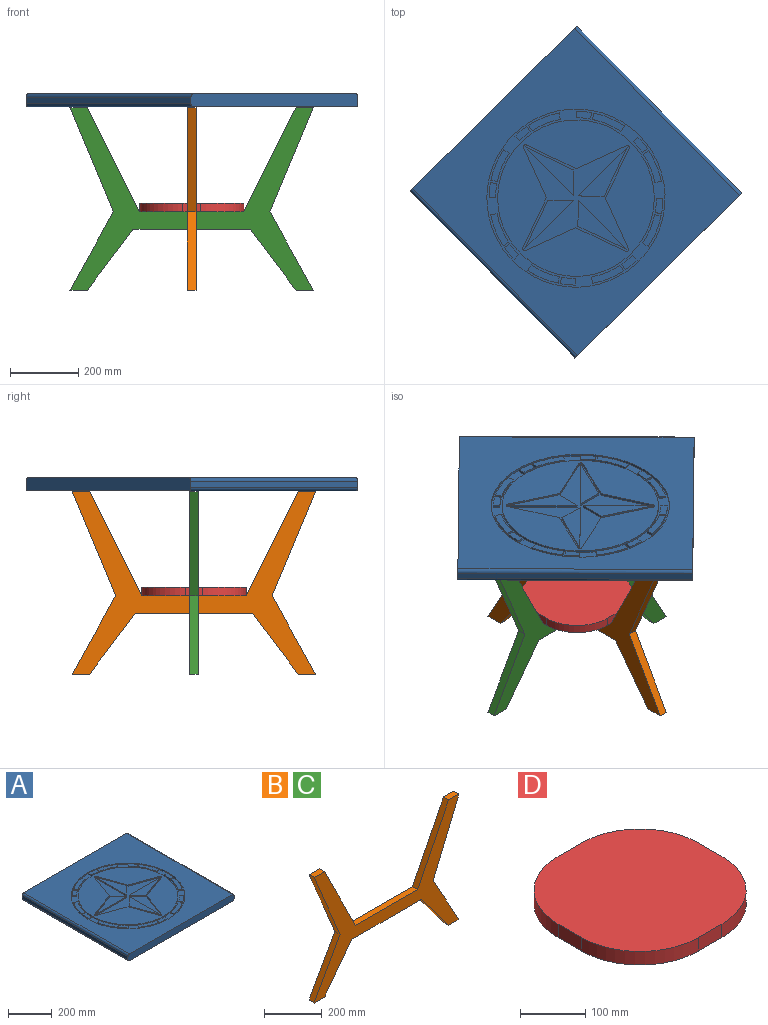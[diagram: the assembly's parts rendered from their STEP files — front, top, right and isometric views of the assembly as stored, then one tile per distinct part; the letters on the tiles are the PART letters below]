
ASSEMBLY  parts=4 mates=2
PART A: 123 faces, bbox 685.8x685.8x38.1 mm
  f0: plane 457.2x457.2mm, normal (0,0,1), area 108640mm2, adj f76,f96,f97,f98,f99,f100,f101,f102
  f1: plane 685.8x666.75mm, normal (0,0,1), area 244313.3mm2, adj f3,f5,f9,f10,f59
  f2: plane 685.8x19.05mm, normal (-1,0,0), area 13064.5mm2, adj f3,f5,f8,f10
  f3: plane 685.8x38.1mm, normal (0,-1,0), area 26051.1mm2, adj f1,f2,f4,f6,f7,f8,f9,f10
  f4: plane 685.8x19.05mm, normal (1,0,0), area 13064.5mm2, adj f3,f5,f7,f9
  f5: plane 685.8x38.1mm, normal (0,1,0), area 26051.1mm2, adj f1,f2,f4,f6,f7,f8,f9,f10
  f6: plane 685.8x666.75mm, normal (0,0,-1), area 457257.1mm2, adj f3,f5,f7,f8
  f7: cylinder r=9.53mm len=685.8mm, axis (0,1,0), area 10260.8mm2, adj f3,f4,f5,f6
  f8: cylinder r=9.53mm len=685.8mm, axis (0,-1,0), area 10260.8mm2, adj f2,f3,f5,f6
  f9: cylinder r=9.53mm len=685.8mm, axis (0,-1,0), area 10260.8mm2, adj f1,f3,f4,f5
  f10: cylinder r=9.53mm len=685.8mm, axis (0,1,0), area 10260.8mm2, adj f1,f2,f3,f5
  f11: cylinder r=254mm len=90.1mm, axis (0,0,1), area 623.1mm2, adj f12,f60,f77,f93
  f12: plane 18.77x6.35mm, normal (0.17,-0.98,0), area 121mm2, adj f11,f13,f77,f93
  f13: cylinder r=234.95mm len=82.47mm, axis (0,0,1), area 570.3mm2, adj f12,f60,f77,f93
  f14: cylinder r=254mm len=33.92mm, axis (0,0,1), area 281.5mm2, adj f15,f61,f77,f92
  f15: plane 15.61x10.93mm, normal (0.57,-0.82,0), area 121mm2, adj f14,f16,f77,f92
  f16: cylinder r=234.95mm len=31.37mm, axis (0,0,1), area 260.4mm2, adj f15,f61,f77,f92
  f17: cylinder r=254mm len=33.92mm, axis (0,0,1), area 281.5mm2, adj f18,f62,f77,f91
  f18: plane 15.61x10.93mm, normal (0.82,0.57,0), area 121mm2, adj f17,f19,f77,f91
  f19: cylinder r=234.95mm len=31.37mm, axis (0,0,1), area 260.4mm2, adj f18,f62,f77,f91
  f20: cylinder r=254mm len=90.1mm, axis (0,0,1), area 623.1mm2, adj f21,f63,f77,f90
  f21: plane 15.61x10.93mm, normal (0.57,0.82,0), area 121mm2, adj f20,f22,f77,f90
  f22: cylinder r=234.95mm len=82.47mm, axis (0,0,1), area 570.3mm2, adj f21,f63,f77,f90
  f23: cylinder r=254mm len=44.11mm, axis (0,0,1), area 281.5mm2, adj f24,f64,f77,f89
  f24: plane 18.76x6.35mm, normal (0.17,0.98,0), area 121mm2, adj f23,f25,f77,f89
  f25: cylinder r=234.95mm len=40.8mm, axis (0,0,1), area 260.4mm2, adj f24,f64,f77,f89
  f26: cylinder r=254mm len=90.1mm, axis (0,0,1), area 623.1mm2, adj f27,f65,f77,f88
  f27: plane 18.77x6.35mm, normal (-0.17,0.98,0), area 121mm2, adj f26,f28,f77,f88
  f28: cylinder r=234.95mm len=82.47mm, axis (0,0,1), area 570.3mm2, adj f27,f65,f77,f88
  f29: cylinder r=254mm len=33.92mm, axis (0,0,1), area 281.5mm2, adj f30,f66,f77,f87
  f30: plane 15.61x10.93mm, normal (-0.57,0.82,0), area 121mm2, adj f29,f31,f77,f87
  f31: cylinder r=234.95mm len=31.37mm, axis (0,0,1), area 260.4mm2, adj f30,f66,f77,f87
  f32: cylinder r=254mm len=90.1mm, axis (0,0,1), area 623.1mm2, adj f33,f67,f77,f86
  f33: plane 15.61x10.93mm, normal (-0.82,0.57,0), area 121mm2, adj f32,f34,f77,f86
  f34: cylinder r=234.95mm len=82.47mm, axis (0,0,1), area 570.3mm2, adj f33,f67,f77,f86
  f35: cylinder r=254mm len=44.11mm, axis (0,0,1), area 281.5mm2, adj f36,f68,f77,f85
  f36: plane 18.76x6.35mm, normal (-0.98,0.17,0), area 121mm2, adj f35,f37,f77,f85
  f37: cylinder r=234.95mm len=40.8mm, axis (0,0,1), area 260.4mm2, adj f36,f68,f77,f85
  f38: cylinder r=254mm len=90.1mm, axis (0,0,1), area 623.1mm2, adj f39,f69,f77,f84
  f39: plane 18.77x6.35mm, normal (-0.98,-0.17,0), area 121mm2, adj f38,f40,f77,f84
  f40: cylinder r=234.95mm len=82.47mm, axis (0,0,1), area 570.3mm2, adj f39,f69,f77,f84
  f41: cylinder r=254mm len=33.92mm, axis (0,0,1), area 281.5mm2, adj f42,f70,f77,f83
  f42: plane 15.61x10.93mm, normal (-0.82,-0.57,0), area 121mm2, adj f41,f43,f77,f83
  f43: cylinder r=234.95mm len=31.37mm, axis (0,0,1), area 260.4mm2, adj f42,f70,f77,f83
  f44: cylinder r=254mm len=90.1mm, axis (0,0,1), area 623.1mm2, adj f45,f71,f77,f82
  f45: plane 15.61x10.93mm, normal (-0.57,-0.82,0), area 121mm2, adj f44,f46,f77,f82
  f46: cylinder r=234.95mm len=82.47mm, axis (0,0,1), area 570.3mm2, adj f45,f71,f77,f82
  f47: cylinder r=254mm len=44.11mm, axis (0,0,1), area 281.5mm2, adj f48,f72,f77,f81
  f48: plane 18.76x6.35mm, normal (-0.17,-0.98,0), area 121mm2, adj f47,f49,f77,f81
  f49: cylinder r=234.95mm len=40.8mm, axis (0,0,1), area 260.4mm2, adj f48,f72,f77,f81
  f50: cylinder r=234.95mm len=82.47mm, axis (0,0,1), area 570.3mm2, adj f51,f73,f77,f80
  f51: plane 18.77x6.35mm, normal (-0.98,0.17,0), area 121mm2, adj f50,f52,f77,f80
  f52: cylinder r=254mm len=90.1mm, axis (0,0,1), area 623.1mm2, adj f51,f73,f77,f80
  f53: plane 18.77x6.35mm, normal (0.98,0.17,0), area 121mm2, adj f54,f74,f77,f79
  f54: cylinder r=234.95mm len=82.47mm, axis (0,0,1), area 570.3mm2, adj f53,f55,f77,f79
  f55: plane 15.61x10.93mm, normal (-0.82,-0.57,0), area 121mm2, adj f54,f74,f77,f79
  f56: cylinder r=234.95mm len=40.8mm, axis (0,0,1), area 260.4mm2, adj f57,f75,f77,f78
  f57: plane 19.05x6.35mm, normal (-1,0,0), area 121mm2, adj f56,f58,f77,f78
  f58: cylinder r=254mm len=44.11mm, axis (0,0,1), area 281.5mm2, adj f57,f75,f77,f78
  f59: cylinder r=260.35mm len=520.7mm, axis (0,0,1), area 10387.5mm2, adj f1,f77
  f60: plane 15.61x10.93mm, normal (-0.57,0.82,0), area 121mm2, adj f11,f13,f77,f93
  f61: plane 13.47x13.47mm, normal (-0.71,0.71,0), area 121mm2, adj f14,f16,f77,f92
  f62: plane 13.47x13.47mm, normal (-0.71,-0.71,0), area 121mm2, adj f17,f19,f77,f91
  f63: plane 18.77x6.35mm, normal (-0.17,-0.98,0), area 121mm2, adj f20,f22,f77,f90
  f64: plane 19.05x6.35mm, normal (0,-1,0), area 121mm2, adj f23,f25,f77,f89
  f65: plane 15.61x10.93mm, normal (0.57,-0.82,0), area 121mm2, adj f26,f28,f77,f88
  f66: plane 13.47x13.47mm, normal (0.71,-0.71,0), area 121mm2, adj f29,f31,f77,f87
  f67: plane 18.77x6.35mm, normal (0.98,-0.17,0), area 121mm2, adj f32,f34,f77,f86
  f68: plane 19.05x6.35mm, normal (1,0,0), area 121mm2, adj f35,f37,f77,f85
  f69: plane 15.61x10.93mm, normal (0.82,0.57,0), area 121mm2, adj f38,f40,f77,f84
  f70: plane 13.47x13.47mm, normal (0.71,0.71,0), area 121mm2, adj f41,f43,f77,f83
  f71: plane 18.77x6.35mm, normal (0.17,0.98,0), area 121mm2, adj f44,f46,f77,f82
  f72: plane 19.05x6.35mm, normal (0,1,0), area 121mm2, adj f47,f49,f77,f81
  f73: plane 15.61x10.93mm, normal (0.82,-0.57,0), area 121mm2, adj f50,f52,f77,f80
  f74: cylinder r=254mm len=90.1mm, axis (0,0,1), area 623.1mm2, adj f53,f55,f77,f79
  f75: plane 18.76x6.35mm, normal (0.98,-0.17,0), area 121mm2, adj f56,f58,f77,f78
  f76: cylinder r=228.6mm len=457.2mm, axis (0,0,1), area 9120.7mm2, adj f0,f77
  f77: plane 520.7x520.7mm, normal (0,0,1), area 27946.7mm2, adj f11,f12,f13,f14,f15,f16,f17,f18
  f78: plane 44.11x22.62mm, normal (0,0,1), area 812.8mm2, adj f56,f57,f58,f75
  f79: plane 93.4x52.93mm, normal (0,0,1), area 1790.1mm2, adj f53,f54,f55,f74
  f80: plane 93.4x52.93mm, normal (0,0,1), area 1790.1mm2, adj f50,f51,f52,f73
  f81: plane 44.11x22.62mm, normal (0,0,1), area 812.8mm2, adj f47,f48,f49,f72
  f82: plane 93.4x52.93mm, normal (0,0,1), area 1790.1mm2, adj f44,f45,f46,f71
  f83: plane 44.84x41.93mm, normal (0,0,1), area 812.8mm2, adj f41,f42,f43,f70
  f84: plane 93.4x52.93mm, normal (0,0,1), area 1790.1mm2, adj f38,f39,f40,f69
  f85: plane 44.11x22.62mm, normal (0,0,1), area 812.8mm2, adj f35,f36,f37,f68
  f86: plane 93.4x52.93mm, normal (0,0,1), area 1790.1mm2, adj f32,f33,f34,f67
  f87: plane 44.84x41.93mm, normal (0,0,1), area 812.8mm2, adj f29,f30,f31,f66
  f88: plane 93.4x52.93mm, normal (0,0,1), area 1790.1mm2, adj f26,f27,f28,f65
  f89: plane 44.11x22.62mm, normal (0,0,1), area 812.8mm2, adj f23,f24,f25,f64
  f90: plane 93.4x52.93mm, normal (0,0,1), area 1790.1mm2, adj f20,f21,f22,f63
  f91: plane 44.84x41.93mm, normal (0,0,1), area 812.8mm2, adj f17,f18,f19,f62
  f92: plane 44.84x41.93mm, normal (0,0,1), area 812.8mm2, adj f14,f15,f16,f61
  f93: plane 93.4x52.93mm, normal (0,0,1), area 1790.1mm2, adj f11,f12,f13,f60
  f94: plane 147.4x53.65mm, normal (-0.34,0.94,0), area 996.1mm2, adj f95,f114,f115,f116
  f95: plane 53.65x53.65mm, normal (0.71,0.71,0), area 481.8mm2, adj f94,f114,f115,f116
  f96: plane 151.2x55.03mm, normal (-0.34,0.94,0), area 1021.8mm2, adj f0,f97,f112,f116
  f97: cylinder r=6.35mm len=11.93mm, axis (0,0,1), area 98.5mm2, adj f0,f96,f98,f116
  f98: plane 151.2x55.03mm, normal (-0.34,-0.94,0), area 1021.8mm2, adj f0,f97,f99,f116
  f99: plane 151.2x55.03mm, normal (-0.94,-0.34,0), area 1021.8mm2, adj f0,f98,f100,f116
  f100: cylinder r=6.35mm len=11.93mm, axis (0,0,1), area 98.5mm2, adj f0,f99,f101,f116
  f101: plane 151.2x55.03mm, normal (0.94,-0.34,0), area 1021.8mm2, adj f0,f100,f102,f116
  f102: plane 151.2x55.03mm, normal (0.34,-0.94,0), area 1021.8mm2, adj f0,f101,f103,f116
  f103: cylinder r=6.35mm len=11.93mm, axis (0,0,1), area 98.5mm2, adj f0,f102,f104,f116
  f104: plane 151.2x55.03mm, normal (0.34,0.94,0), area 1021.8mm2, adj f0,f103,f105,f116
  f105: plane 151.2x55.03mm, normal (0.94,0.34,0), area 1021.8mm2, adj f0,f104,f106,f116
  f106: cylinder r=6.35mm len=11.93mm, axis (0,0,1), area 98.5mm2, adj f0,f105,f112,f116
  f107: plane 147.4x53.65mm, normal (-0.94,-0.34,0), area 996.1mm2, adj f108,f116,f117,f118
  f108: plane 53.65x53.65mm, normal (-0.71,0.71,0), area 481.8mm2, adj f107,f116,f117,f118
  f109: plane 147.4x53.65mm, normal (0.34,-0.94,0), area 996.1mm2, adj f113,f116,f119,f120
  f110: plane 147.4x53.65mm, normal (0.94,0.34,0), area 996.1mm2, adj f111,f116,f121,f122
  f111: plane 53.65x53.65mm, normal (0.71,-0.71,0), area 481.8mm2, adj f110,f116,f121,f122
  f112: plane 151.2x55.03mm, normal (-0.94,0.34,0), area 1021.8mm2, adj f0,f96,f106,f116
  f113: plane 53.65x53.65mm, normal (-0.71,-0.71,0), area 481.8mm2, adj f109,f116,f119,f120
  f114: plane 201.05x53.65mm, normal (0,0,1), area 5393.3mm2, adj f94,f95,f115
  f115: plane 201.05x6.35mm, normal (0,-1,0), area 1276.7mm2, adj f94,f95,f114,f116
  f116: plane 432.77x432.77mm, normal (0,0,1), area 33960.1mm2, adj f94,f95,f96,f97,f98,f99,f100,f101
  f117: plane 201.05x53.65mm, normal (0,0,1), area 5393.3mm2, adj f107,f108,f118
  f118: plane 201.05x6.35mm, normal (1,0,0), area 1276.7mm2, adj f107,f108,f116,f117
  f119: plane 201.05x53.65mm, normal (0,0,1), area 5393.3mm2, adj f109,f113,f120
  f120: plane 201.05x6.35mm, normal (0,1,0), area 1276.7mm2, adj f109,f113,f116,f119
  f121: plane 201.05x53.65mm, normal (0,0,1), area 5393.3mm2, adj f110,f111,f122
  f122: plane 201.05x6.35mm, normal (-1,0,0), area 1276.7mm2, adj f110,f111,f116,f121
PART B: 16 faces, bbox 711.2x25.4x533.4 mm
  f0: plane 304.8x127mm, normal (-0.92,0,-0.38), area 8387.1mm2, adj f1,f13,f14,f15
  f1: plane 228.6x127mm, normal (-0.87,0,0.49), area 6642.3mm2, adj f0,f2,f14,f15
  f2: plane 50.8x25.4mm, normal (0,0,-1), area 1290.3mm2, adj f1,f3,f14,f15
  f3: plane 177.8x133.35mm, normal (0.8,0,-0.6), area 5645.2mm2, adj f2,f4,f14,f15
  f4: plane 342.9x25.4mm, normal (0,0,-1), area 8709.7mm2, adj f3,f5,f14,f15
  f5: plane 177.8x133.35mm, normal (-0.8,0,-0.6), area 5645.2mm2, adj f4,f6,f14,f15
  f6: plane 50.8x25.4mm, normal (0,0,-1), area 1290.3mm2, adj f5,f7,f14,f15
  f7: plane 228.6x127mm, normal (0.87,0,0.49), area 6642.3mm2, adj f6,f8,f14,f15
  f8: plane 304.8x127mm, normal (0.92,0,-0.38), area 8387.1mm2, adj f7,f9,f14,f15
  f9: plane 50.8x25.4mm, normal (0,0,1), area 1290.3mm2, adj f8,f10,f14,f15
  f10: plane 304.8x152.4mm, normal (-0.89,0,0.45), area 8655.7mm2, adj f9,f11,f14,f15
  f11: plane 304.8x25.4mm, normal (0,0,1), area 7741.9mm2, adj f10,f12,f14,f15
  f12: plane 304.8x152.4mm, normal (0.89,0,0.45), area 8655.7mm2, adj f11,f13,f14,f15
  f13: plane 50.8x25.4mm, normal (0,0,1), area 1290.3mm2, adj f0,f12,f14,f15
  f14: plane 711.2x533.4mm, normal (0,-1,0), area 87580.5mm2, adj f0,f1,f2,f3,f4,f5,f6,f7
  f15: plane 711.2x533.4mm, normal (0,1,0), area 87580.5mm2, adj f0,f1,f2,f3,f4,f5,f6,f7
PART C: same geometry as B
PART D: 10 faces, bbox 304.8x304.8x25.4 mm
  f0: plane 50.8x25.4mm, normal (-1,0,0), area 1290.3mm2, adj f4,f5,f6,f9
  f1: plane 50.8x25.4mm, normal (0,-1,0), area 1290.3mm2, adj f4,f5,f6,f7
  f2: plane 50.8x25.4mm, normal (1,0,0), area 1290.3mm2, adj f4,f5,f7,f8
  f3: plane 50.8x25.4mm, normal (0,1,0), area 1290.3mm2, adj f4,f5,f8,f9
  f4: plane 304.8x304.8mm, normal (0,0,1), area 79057.8mm2, adj f0,f1,f2,f3,f6,f7,f8,f9
  f5: plane 304.8x304.8mm, normal (0,0,-1), area 79057.8mm2, adj f0,f1,f2,f3,f6,f7,f8,f9
  f6: cylinder r=127mm len=127mm, axis (0,0,1), area 5067.1mm2, adj f0,f1,f4,f5
  f7: cylinder r=127mm len=127mm, axis (0,0,-1), area 5067.1mm2, adj f1,f2,f4,f5
  f8: cylinder r=127mm len=127mm, axis (0,0,1), area 5067.1mm2, adj f2,f3,f4,f5
  f9: cylinder r=127mm len=127mm, axis (0,0,-1), area 5067.1mm2, adj f0,f3,f4,f5
PLACE A rot(axis=(0,0,1),44.6deg) t=(51.37,101.09,442.86)mm
PLACE B rot(axis=(0,0,-1),90deg) t=(50.52,469.14,-92.55)mm
PLACE C t=(-305.08,113.54,-92.55)mm
PLACE D t=(-101.88,-38.86,136.05)mm
MATE fastened C.f4 <-> B.f4  axis (0,0,-1) through (50.52,113.54,85.25)mm
MATE fastened D.f5 <-> B.f11  axis (0,0,-1) through (50.52,113.54,136.05)mm
